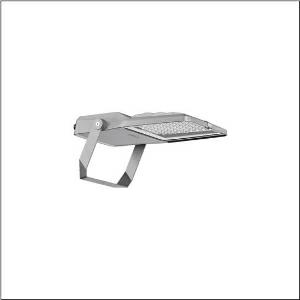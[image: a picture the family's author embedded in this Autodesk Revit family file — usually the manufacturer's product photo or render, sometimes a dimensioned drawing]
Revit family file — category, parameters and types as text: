
# Revit family: floodlight_fl_21_mini___pl33t_5xa7776b2f1a_8d7b
name_source: partatom
category: Lighting Fixtures
units: mm (PartAtom-declared; Revit-internal decimal feet)

## family parameters
Cut with Voids When Loaded = No
Host = Face
Light Source = No
Part Type = Normal
Room Calculation Point = No
Round Connector Dimension = Use Diameter
Shared = No

## types (1)
- --- (1 x LED, 6150 lm, 45.7 W, 3000K)
    Apparent Load = 46 VA
    CIE Flux Codes = 26 75 99 100 100
    Color Rendering = 70
    Color Temperature = 3000K
    Default Elevation = 1800 mm
    Description = Floodlight FL 21 mini, floodlight, primary light control with lens, of PMMA, primary optical cover: protective disc, of toughened safety glass, transparent, light distribution: PL33T, light emission: direct distribution, installation type: surface-mounted, LED, High Power LED, rated luminous flux: 6.150lm, luminous efficacy: 135lm/W, light colour: 730, colour temperature: 3000K, control gear: Smart Interface (Zhaga), control: flexible luminous flux parameterisation, time-dependent luminous flux control, constant luminous flux control, overheat protection, pre-setting: logarithmic dimming characteristic, with terminal, 6-pole, mains connection: 220..240V, AC, 50/60Hz, start of lifetime: 46W, end of service life: 48W, reduction: 22W, luminaire housing, of diecast aluminium, powder-coated, SITECO metallic grey (DB 702S), corrosivity category C5 mid according to DIN EN ISO 12944, suitable for swimming pools, chlorine-resistant, sealing non-destructively replaceable, mounting bracket, of steel, galvanised, powder-coated, SITECO metallic grey (DB 702S), Smart Interface below and above, protection rating (complete): IP66, insulation class (complete): insulation class II (safety insulation), certification: CE, ENEC, VDE, protection symbol: D, impact resistance: IK08, permissible operating ambient temperature: -40..+40°C, permissible operating ambient temperature for outdoor applications: -40..+50°C, standard: DIN EN 12944, LABS conformity tested according to VDMA 24364:2018-05, packaging unit: 1 piece

Light Distribution: PL33T
    Height = 70 mm
    Lamp = 1 x LED
    Lamp Light Flux = 6150 lm
    Lamp Power = 45.7 W
    Lamp count = 1
    Length = 485 mm
    Luminous efficacy = 135 lm/W
    Manufacturer = Siteco
    ModVariant = No
    Model = 5XA7776B2F1A
    Number of Poles = 1
    OnlyDefault = Yes
    Power Factor = 1
    Product Name = Floodlight FL 21 mini | PL33T
    Product group = floodlight | pylon annexe
    ProductGroupID = 6201
    Protection Class = Protection class II
    Protection Degree = IP 66
    RLX_Detail_Level = 1
    RLX_Emergency_Light_Flux = 0 lm
    RLX_Emergency_Type = 0
    RLX_Emergency_Type_DB = No
    RlxData = <blob elided: 95949 chars, md5=3881765a>
    Socket = socket
    Standby Power = 0 W
    System Light Flux = 6150 lm
    System Power = 46 W
    Type Comments = factory setting: luminous flux: 100 % | dim-lin: 254 | 463 mA
    Type Image = l_1006845.jpg
    URL = http://relux.com
    VarID = @adj_148135
    Voltage = 0 V
    Weight = 0.00 kg
    Width = 337 mm

## geometry (parser evidence)
native form markers: Blend x4, Sweep x12
no freeform markers — native parametric forms only
